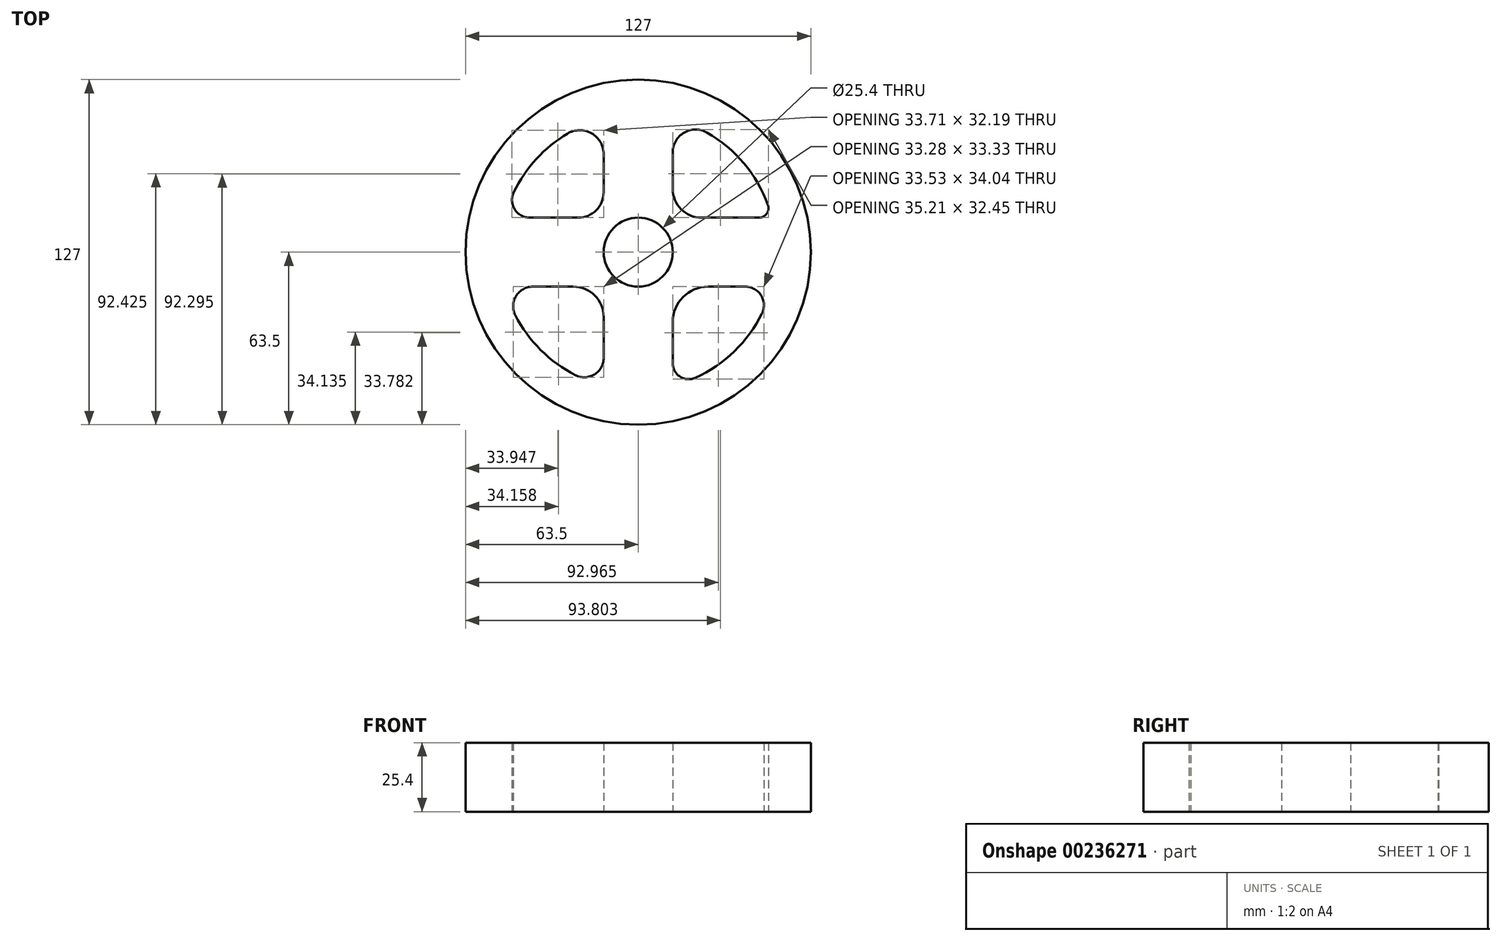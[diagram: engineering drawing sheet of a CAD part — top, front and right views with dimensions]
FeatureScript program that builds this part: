
annotation { "Feature Type Name" : "Feature", "Feature Type Description" : "" }
export const myFeature = defineFeature(function(context is Context, id is Id, definition is map)
    precondition{}
    {
        {
            var Q0;
            Q0=qCreatedBy(makeId("Top.planeOp"),FACE);
            var sketch = newSketch(context, id + "F0", { "sketchPlane" : qUnion([Q0])});
            skArc(sketch, "E0", {"start": v(-25.98, 43.66) * mm, "mid": v(-37.47, 34.3) * mm, "end": v(-45.77, 22.04) * mm});
            skCircle(sketch, "E1", {"center": v(0, 0) * mm, "radius": 63.5 * mm});
            skCircle(sketch, "E2", {"center": v(0, 0) * mm, "radius": 12.7 * mm});
            skLineSegment(sketch, "E3", {"start": v(0, 0) * mm, "end": v(0, 50.8) * mm});
            skLineSegment(sketch, "E4.0", {"start": v(12.7, 23.3) * mm, "end": v(12.7, 36.71) * mm});
            skLineSegment(sketch, "E5.0", {"start": v(-12.7, 22.05) * mm, "end": v(-12.7, 36.1) * mm});
            skLineSegment(sketch, "E6", {"start": v(0, 0) * mm, "end": v(0, -50.8) * mm});
            skLineSegment(sketch, "E7", {"start": v(0, 0) * mm, "end": v(50.8, 0) * mm});
            skLineSegment(sketch, "E8", {"start": v(0, 0) * mm, "end": v(-50.8, 0) * mm});
            skLineSegment(sketch, "E9.0", {"start": v(-22.05, 12.7) * mm, "end": v(-39.9, 12.7) * mm});
            skLineSegment(sketch, "E10.0", {"start": v(-23.82, -12.7) * mm, "end": v(-38.78, -12.7) * mm});
            skLineSegment(sketch, "E11.0", {"start": v(23.3, 12.7) * mm, "end": v(44.4, 12.7) * mm});
            skLineSegment(sketch, "E12.0", {"start": v(25.7, -12.7) * mm, "end": v(39.43, -12.7) * mm});
            skLineSegment(sketch, "E13.0", {"start": v(12.7, -25.7) * mm, "end": v(12.7, -40.83) * mm});
            skLineSegment(sketch, "E14.0", {"start": v(-12.7, -23.82) * mm, "end": v(-12.7, -38.9) * mm});
            skLineSegment(sketch, "E15.trimOffspring", {"start": v(62.22, 12.7) * mm, "end": v(63.5, 12.7) * mm});
            skLineSegment(sketch, "E16.trimOffspring", {"start": v(62.22, -12.7) * mm, "end": v(63.5, -12.7) * mm});
            skLineSegment(sketch, "E17.trimOffspring", {"start": v(-12.7, -62.22) * mm, "end": v(-12.7, -63.5) * mm});
            skLineSegment(sketch, "E18.trimOffspring", {"start": v(-62.22, -12.7) * mm, "end": v(-63.5, -12.7) * mm});
            skLineSegment(sketch, "E19.trimOffspring", {"start": v(-62.22, 12.7) * mm, "end": v(-63.5, 12.7) * mm});
            skLineSegment(sketch, "E20.trimOffspring", {"start": v(-12.7, 62.22) * mm, "end": v(-12.7, 63.5) * mm});
            skLineSegment(sketch, "E21.trimOffspring", {"start": v(12.7, 62.22) * mm, "end": v(12.7, 63.5) * mm});
            skLineSegment(sketch, "E22.trimOffspring", {"start": v(12.7, -62.22) * mm, "end": v(12.7, -63.5) * mm});
            skArc(sketch, "E23.trimOffspring", {"start": v(-45.2, -23.2) * mm, "mid": v(-35.87, -35.97) * mm, "end": v(-23.07, -45.26) * mm});
            skArc(sketch, "E24.trimOffspring", {"start": v(21.09, -46.22) * mm, "mid": v(35.35, -36.48) * mm, "end": v(45.53, -22.53) * mm});
            skArc(sketch, "E25.trimOffspring", {"start": v(47.71, 17.44) * mm, "mid": v(38.87, 32.7) * mm, "end": v(25.35, 44.02) * mm});
            skPoint(sketch, "E26.visualSharp", {"position": v(-12.7, 12.7) * mm});
            skArc(sketch, "E26.filletArc", {"start": v(-22.05, 12.7) * mm, "mid": v(-15.44, 15.44) * mm, "end": v(-12.7, 22.05) * mm});
            skPoint(sketch, "E27.visualSharp", {"position": v(12.7, 12.7) * mm});
            skArc(sketch, "E27.filletArc", {"start": v(12.7, 23.3) * mm, "mid": v(15.8, 15.8) * mm, "end": v(23.3, 12.7) * mm});
            skPoint(sketch, "E28.visualSharp", {"position": v(-12.7, -12.7) * mm});
            skArc(sketch, "E28.filletArc", {"start": v(-12.7, -23.82) * mm, "mid": v(-15.96, -15.96) * mm, "end": v(-23.82, -12.7) * mm});
            skPoint(sketch, "E29.visualSharp", {"position": v(12.7, -12.7) * mm});
            skArc(sketch, "E29.filletArc", {"start": v(25.7, -12.7) * mm, "mid": v(16.5, -16.5) * mm, "end": v(12.7, -25.7) * mm});
            skPoint(sketch, "E30.visualSharp", {"position": v(-12.7, 49.19) * mm});
            skArc(sketch, "E30.filletArc", {"start": v(-12.7, 36.1) * mm, "mid": v(-17.14, 43.74) * mm, "end": v(-25.98, 43.66) * mm});
            skPoint(sketch, "E31.visualSharp", {"position": v(12.7, 49.19) * mm});
            skArc(sketch, "E31.filletArc", {"start": v(25.35, 44.02) * mm, "mid": v(16.91, 44.02) * mm, "end": v(12.7, 36.71) * mm});
            skPoint(sketch, "E32.visualSharp", {"position": v(-49.19, 12.7) * mm});
            skArc(sketch, "E32.filletArc", {"start": v(-45.77, 22.04) * mm, "mid": v(-45.42, 15.75) * mm, "end": v(-39.9, 12.7) * mm});
            skPoint(sketch, "E33.visualSharp", {"position": v(-49.19, -12.7) * mm});
            skArc(sketch, "E33.filletArc", {"start": v(-38.78, -12.7) * mm, "mid": v(-44.93, -16.15) * mm, "end": v(-45.2, -23.2) * mm});
            skPoint(sketch, "E34.visualSharp", {"position": v(-12.7, -49.19) * mm});
            skArc(sketch, "E34.filletArc", {"start": v(-23.07, -45.26) * mm, "mid": v(-16.1, -44.99) * mm, "end": v(-12.7, -38.9) * mm});
            skPoint(sketch, "E35.visualSharp", {"position": v(12.7, -49.19) * mm});
            skArc(sketch, "E35.filletArc", {"start": v(12.7, -40.83) * mm, "mid": v(15.42, -45.81) * mm, "end": v(21.09, -46.22) * mm});
            skPoint(sketch, "E36.visualSharp", {"position": v(49.19, -12.7) * mm});
            skArc(sketch, "E36.filletArc", {"start": v(45.53, -22.53) * mm, "mid": v(45.21, -15.92) * mm, "end": v(39.43, -12.7) * mm});
            skPoint(sketch, "E37.startSnap0", {"position": v(-17.14, 43.74) * mm});
            skPoint(sketch, "E38.visualSharp", {"position": v(49.19, 12.7) * mm});
            skArc(sketch, "E38.filletArc", {"start": v(44.4, 12.7) * mm, "mid": v(47.29, 14.2) * mm, "end": v(47.71, 17.44) * mm});
            skSolve(sketch);
        }
        {
            var Q0;
            Q0 = qSketchRegion(id + "F0", true);
            extrude(context, id + "F1", {"entities" : qUnion([Q0]), "depth" : 25.4 * mm});
        }
    });
